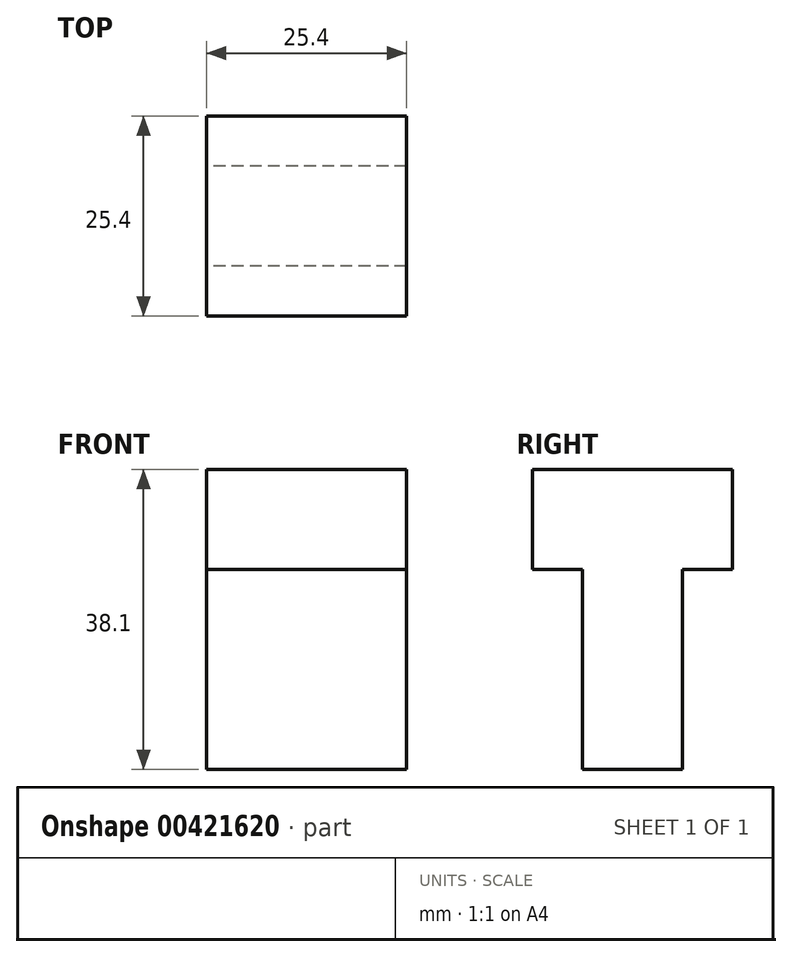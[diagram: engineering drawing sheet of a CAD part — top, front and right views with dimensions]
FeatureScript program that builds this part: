
annotation { "Feature Type Name" : "Feature", "Feature Type Description" : "" }
export const myFeature = defineFeature(function(context is Context, id is Id, definition is map)
    precondition{}
    {
        {
            var Q0;
            Q0=qCreatedBy(makeId("Right.planeOp"),FACE);
            var sketch = newSketch(context, id + "F0", { "sketchPlane" : qUnion([Q0])});
            skLineSegment(sketch, "E0", {"start": v(0, 0) * mm, "end": v(0, 25.4) * mm});
            skLineSegment(sketch, "E1", {"start": v(0, 25.4) * mm, "end": v(-6.35, 25.4) * mm});
            skLineSegment(sketch, "E2", {"start": v(-6.35, 25.4) * mm, "end": v(-6.35, 38.1) * mm});
            skLineSegment(sketch, "E3", {"start": v(-6.35, 38.1) * mm, "end": v(19.05, 38.1) * mm});
            skLineSegment(sketch, "E4", {"start": v(19.05, 38.1) * mm, "end": v(19.05, 25.4) * mm});
            skLineSegment(sketch, "E5", {"start": v(19.05, 25.4) * mm, "end": v(12.7, 25.4) * mm});
            skLineSegment(sketch, "E6", {"start": v(12.7, 25.4) * mm, "end": v(12.7, 0) * mm});
            skLineSegment(sketch, "E7", {"start": v(12.7, 0) * mm, "end": v(0, 0) * mm});
            skSolve(sketch);
        }
        {
            var Q0;
            Q0=makeQuery(id+"F0.imprint","IMPRINT",FACE,{"disambiguationData":[TD([[makeQuery(id+"F0.imprint","IMPRINT",EDGE,{"derivedFrom":sQuery(id+"F0.wireOp",EDGE,"E0")}),-1.0]])]});
            extrude(context, id + "F1", {"entities" : qUnion([Q0]), "depth" : 25.4 * mm});
        }
    });
